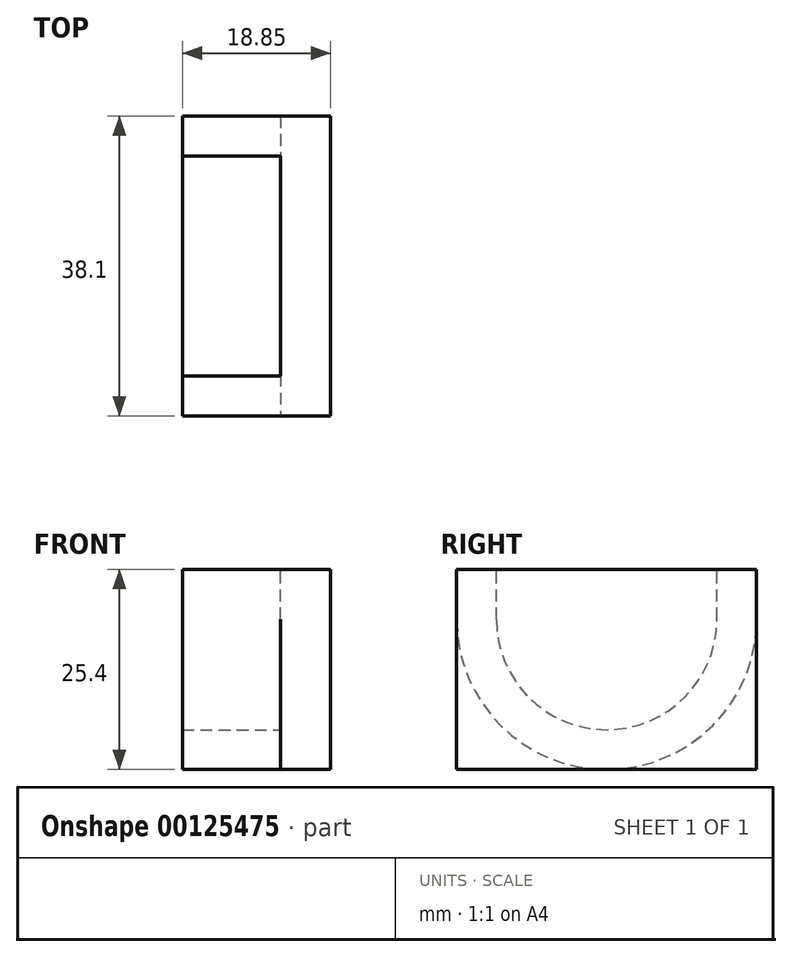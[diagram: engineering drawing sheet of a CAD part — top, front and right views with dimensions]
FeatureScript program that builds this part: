
annotation { "Feature Type Name" : "Feature", "Feature Type Description" : "" }
export const myFeature = defineFeature(function(context is Context, id is Id, definition is map)
    precondition{}
    {
        {
            var Q0;
            Q0=qCreatedBy(makeId("Top.planeOp"),FACE);
            var sketch = newSketch(context, id + "F0", { "sketchPlane" : qUnion([Q0])});
            skLineSegment(sketch, "E0.bottom", {"start": v(-6.35, 19.05) * mm, "end": v(0, 19.05) * mm});
            skLineSegment(sketch, "E0.top", {"start": v(-6.35, -19.05) * mm, "end": v(0, -19.05) * mm});
            skLineSegment(sketch, "E0.left", {"start": v(-6.35, 19.05) * mm, "end": v(-6.35, -19.05) * mm});
            skLineSegment(sketch, "E0.right", {"start": v(0, 19.05) * mm, "end": v(0, -19.05) * mm});
            skSolve(sketch);
        }
        {
            var Q0;
            Q0=qSketchRegion(id+"F0",true);
            extrude(context, id + "F1", {"entities" : qUnion([Q0]), "depth" : 25.4 * mm});
        }
        {
            var Q0;
            Q0=makeQuery(id+"F1.opExtrude","SWEPT_FACE",FACE,{"disambiguationData":[OSD([sQuery(id+"F0.wireOp",EDGE,"E0.left")])]});
            var sketch = newSketch(context, id + "F2", { "sketchPlane" : qUnion([Q0])});
            skArc(sketch, "E1", {"start": v(-19.05, 19.05) * mm, "mid": v(0, 0) * mm, "end": v(19.05, 19.05) * mm});
            skLineSegment(sketch, "E2", {"start": v(-19.05, 19.05) * mm, "end": v(19.05, 19.05) * mm, "construction": true});
            skLineSegment(sketch, "E3", {"start": v(-19.05, 19.05) * mm, "end": v(-19.05, 25.4) * mm});
            skLineSegment(sketch, "E4", {"start": v(19.05, 19.05) * mm, "end": v(19.05, 25.4) * mm});
            skArc(sketch, "E5", {"start": v(-14, 19.05) * mm, "mid": v(0, 5.05) * mm, "end": v(14, 19.05) * mm});
            skLineSegment(sketch, "E6", {"start": v(-14, 19.05) * mm, "end": v(-14, 25.4) * mm});
            skLineSegment(sketch, "E7", {"start": v(-14, 25.4) * mm, "end": v(-19.05, 25.4) * mm});
            skLineSegment(sketch, "E8", {"start": v(14, 19.05) * mm, "end": v(14, 25.4) * mm});
            skLineSegment(sketch, "E9", {"start": v(14, 25.4) * mm, "end": v(19.05, 25.4) * mm});
            skSolve(sketch);
        }
        {
            var Q0;
            Q0=qSketchRegion(id+"F2",true);
            extrude(context, id + "F3", {"entities" : qUnion([Q0]), "operationType" : NewBodyOperationType.ADD, "depth" : 12.5 * mm});
        }
    });
